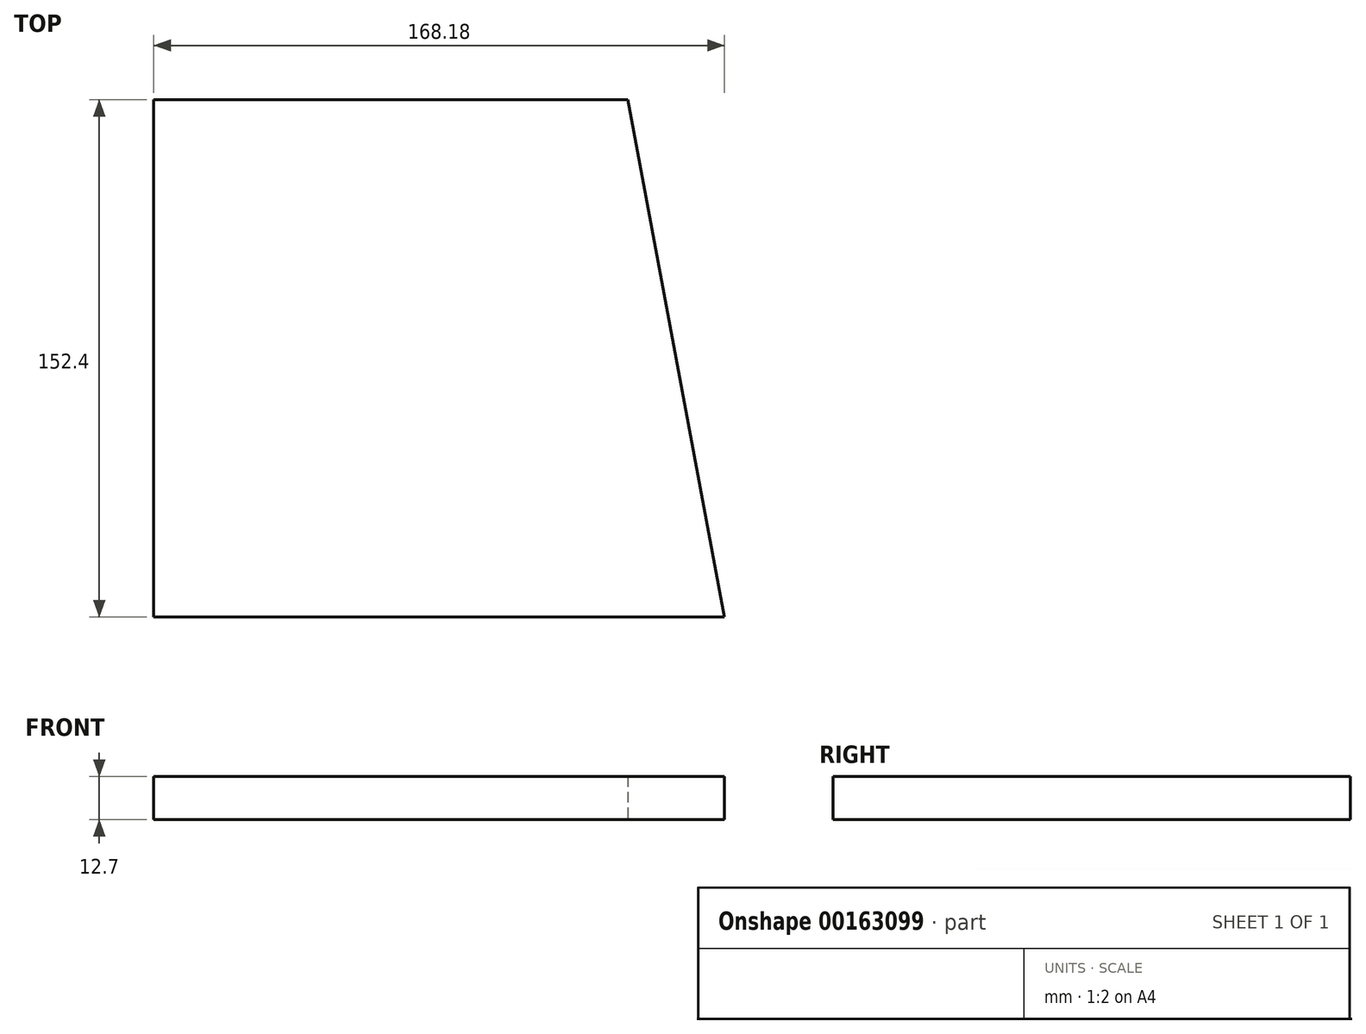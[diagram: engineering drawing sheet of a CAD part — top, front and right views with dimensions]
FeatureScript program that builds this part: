
annotation { "Feature Type Name" : "Feature", "Feature Type Description" : "" }
export const myFeature = defineFeature(function(context is Context, id is Id, definition is map)
    precondition{}
    {
        {
            var Q0;
            Q0=qCreatedBy(makeId("Top.planeOp"),FACE);
            var sketch = newSketch(context, id + "F0", { "sketchPlane" : qUnion([Q0])});
            skLineSegment(sketch, "E0", {"start": v(-79.26, 60.16) * mm, "end": v(-79.26, -92.24) * mm});
            skLineSegment(sketch, "E1", {"start": v(-79.26, -92.24) * mm, "end": v(88.92, -92.24) * mm});
            skLineSegment(sketch, "E2", {"start": v(88.92, -92.24) * mm, "end": v(60.44, 60.16) * mm});
            skLineSegment(sketch, "E3", {"start": v(60.44, 60.16) * mm, "end": v(-79.26, 60.16) * mm});
            skSolve(sketch);
        }
        {
            var Q0;
            Q0=makeQuery(id+"F0.imprint","IMPRINT",FACE,{"disambiguationData":[TD([[makeQuery(id+"F0.imprint","IMPRINT",EDGE,{"derivedFrom":sQuery(id+"F0.wireOp",EDGE,"E0")}),1.0]])]});
            extrude(context, id + "F1", {"entities" : qUnion([Q0]), "depth" : 12.7 * mm});
        }
    });
